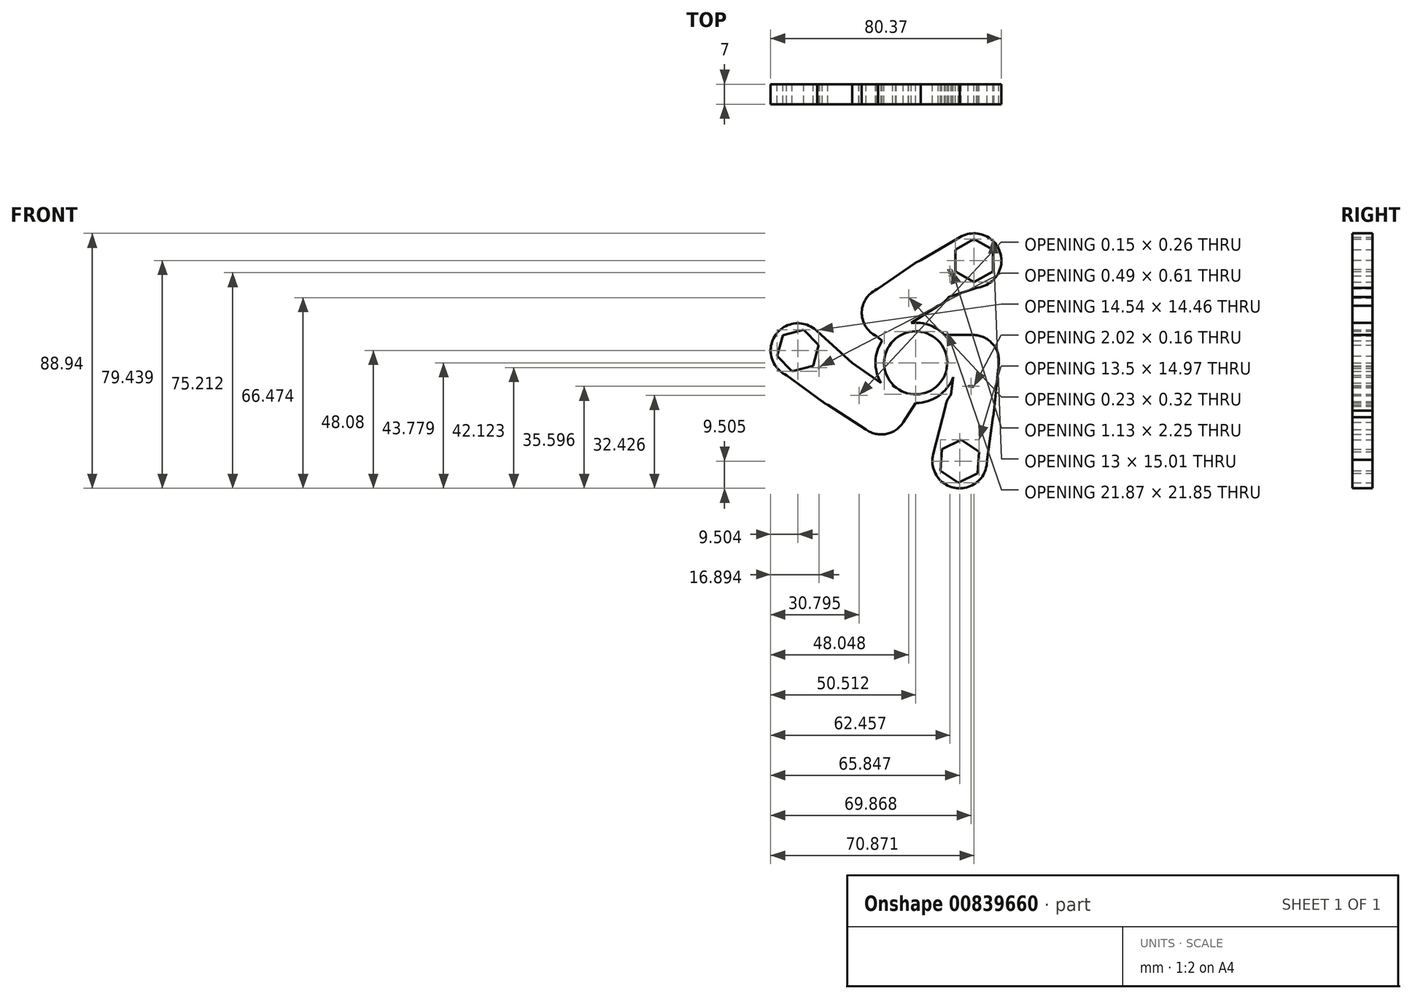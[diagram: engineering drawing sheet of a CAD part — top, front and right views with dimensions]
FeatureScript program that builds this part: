
annotation { "Feature Type Name" : "Feature", "Feature Type Description" : "" }
export const myFeature = defineFeature(function(context is Context, id is Id, definition is map)
    precondition{}
    {
        {
            var Q0;
            Q0=qCreatedBy(makeId("Front.planeOp"),FACE);
            var sketch = newSketch(context, id + "F0", { "sketchPlane" : qUnion([Q0])});
            skCircle(sketch, "E0", {"center": v(0, 0) * mm, "radius": 11 * mm});
            skCircle(sketch, "E1", {"center": v(0, 0) * mm, "radius": 14 * mm});
            skCircle(sketch, "E2", {"center": v(-12, -15.97) * mm, "radius": 9 * mm});
            skPoint(sketch, "E2.first.point", {"position": v(-3.32, -13.6) * mm});
            skPoint(sketch, "E2.second.point", {"position": v(-12.14, -6.97) * mm});
            skPoint(sketch, "E2.third.point", {"position": v(-19.3, -10.7) * mm});
            skCircle(sketch, "E3", {"center": v(-27.02, -6.98) * mm, "radius": 8.5 * mm});
            skPoint(sketch, "E3.first.point", {"position": v(-19.65, -11.22) * mm});
            skPoint(sketch, "E3.second.point", {"position": v(-19.8, -11.47) * mm});
            skPoint(sketch, "E3.third.point", {"position": v(-19.3, -3.4) * mm});
            skLineSegment(sketch, "E4", {"start": v(-12.14, -6.97) * mm, "end": v(-22.16, 0) * mm});
            skLineSegment(sketch, "E5", {"start": v(-4.35, -20.7) * mm, "end": v(0, -14) * mm});
            skCircle(sketch, "E6", {"center": v(19.99, 0.74) * mm, "radius": 9 * mm});
            skPoint(sketch, "E6.first.point", {"position": v(12.66, 5.97) * mm});
            skPoint(sketch, "E6.second.point", {"position": v(13.07, -5.02) * mm});
            skPoint(sketch, "E6.third.point", {"position": v(20.36, -8.25) * mm});
            skCircle(sketch, "E7", {"center": v(18.75, -16.6) * mm, "radius": 8.5 * mm});
            skPoint(sketch, "E7.second.point", {"position": v(12.37, -10.97) * mm});
            skPoint(sketch, "E7.third.point", {"position": v(20.36, -24.94) * mm});
            skLineSegment(sketch, "E8", {"start": v(13.07, -5.02) * mm, "end": v(12.37, -10.97) * mm});
            skLineSegment(sketch, "E9", {"start": v(27.25, -16.6) * mm, "end": v(28.96, 0) * mm});
            skLineSegment(sketch, "E10", {"start": v(0, 0) * mm, "end": v(-17.27, -23.27) * mm});
            skLineSegment(sketch, "E11", {"start": v(-17.27, -23.27) * mm, "end": v(-32.51, -13.46) * mm});
            skLineSegment(sketch, "E12", {"start": v(19.99, 0.74) * mm, "end": v(19.99, 9.74) * mm});
            skLineSegment(sketch, "E13", {"start": v(19.99, 9.74) * mm, "end": v(10.05, 9.74) * mm});
            skCircle(sketch, "E14", {"center": v(-9.78, 17.45) * mm, "radius": 9 * mm});
            skPoint(sketch, "E14.first.point", {"position": v(-11.09, 8.54) * mm});
            skPoint(sketch, "E14.second.point", {"position": v(-1.5, 13.92) * mm});
            skPoint(sketch, "E14.third.point", {"position": v(-11.33, 26.31) * mm});
            skCircle(sketch, "E15", {"center": v(4.42, 27.67) * mm, "radius": 8.5 * mm});
            skPoint(sketch, "E15.first.point", {"position": v(-2.59, 22.86) * mm});
            skPoint(sketch, "E15.second.point", {"position": v(7.8, 19.87) * mm});
            skPoint(sketch, "E15.third.point", {"position": v(12.92, 27.48) * mm});
            skLineSegment(sketch, "E16", {"start": v(7.8, 19.87) * mm, "end": v(-1.5, 13.92) * mm});
            skLineSegment(sketch, "E17", {"start": v(-16.53, 23.4) * mm, "end": v(0, 34.95) * mm});
            skLineSegment(sketch, "E18", {"start": v(-16.92, 11.98) * mm, "end": v(-11.68, 7.72) * mm});
            skCircle(sketch, "E19", {"center": v(15.33, -34.27) * mm, "radius": 9.5 * mm});
            skPoint(sketch, "E19.first.point", {"position": v(17.13, -24.94) * mm});
            skPoint(sketch, "E19.second.point", {"position": v(13.52, -24.94) * mm});
            skPoint(sketch, "E19.third.point", {"position": v(21.46, -41.52) * mm});
            skLineSegment(sketch, "E20", {"start": v(10.36, -15.19) * mm, "end": v(6.12, -31.93) * mm});
            skLineSegment(sketch, "E21", {"start": v(26.93, -18.9) * mm, "end": v(24.31, -37.35) * mm});
            skCircle(sketch, "E22.cCircle", {"center": v(15.33, -34.27) * mm, "radius": 6.5 * mm, "construction": true});
            skLineSegment(sketch, "E22.0", {"start": v(21.55, -38.47) * mm, "end": v(14.8, -41.75) * mm});
            skLineSegment(sketch, "E22.1", {"start": v(14.8, -41.75) * mm, "end": v(8.58, -37.55) * mm});
            skLineSegment(sketch, "E22.2", {"start": v(8.58, -37.55) * mm, "end": v(9.1, -30.06) * mm});
            skLineSegment(sketch, "E22.3", {"start": v(9.1, -30.06) * mm, "end": v(15.86, -26.78) * mm});
            skLineSegment(sketch, "E22.4", {"start": v(15.86, -26.78) * mm, "end": v(22.08, -30.98) * mm});
            skLineSegment(sketch, "E22.5", {"start": v(22.08, -30.98) * mm, "end": v(21.55, -38.47) * mm});
            skPoint(sketch, "E22.0.midPoint", {"position": v(18.17, -40.11) * mm});
            skCircle(sketch, "E23", {"center": v(-41.02, 4.31) * mm, "radius": 9.5 * mm});
            skPoint(sketch, "E23.first.point", {"position": v(-33.87, -1.95) * mm});
            skPoint(sketch, "E23.second.point", {"position": v(-32.06, 7.5) * mm});
            skPoint(sketch, "E23.third.point", {"position": v(-46.5, 12.06) * mm});
            skLineSegment(sketch, "E24", {"start": v(-48.07, -2.05) * mm, "end": v(-32.51, -13.46) * mm});
            skLineSegment(sketch, "E25", {"start": v(-34.3, 11.03) * mm, "end": v(-22.16, 0) * mm});
            skCircle(sketch, "E26.cCircle", {"center": v(-41.02, 4.31) * mm, "radius": 6.5 * mm, "construction": true});
            skLineSegment(sketch, "E26.0", {"start": v(-48.28, 2.44) * mm, "end": v(-46.27, 9.67) * mm});
            skLineSegment(sketch, "E26.1", {"start": v(-46.27, 9.67) * mm, "end": v(-39, 11.54) * mm});
            skLineSegment(sketch, "E26.2", {"start": v(-39, 11.54) * mm, "end": v(-33.75, 6.19) * mm});
            skLineSegment(sketch, "E26.3", {"start": v(-33.75, 6.19) * mm, "end": v(-35.76, -1.05) * mm});
            skLineSegment(sketch, "E26.4", {"start": v(-35.76, -1.05) * mm, "end": v(-43.03, -2.92) * mm});
            skLineSegment(sketch, "E26.5", {"start": v(-43.03, -2.92) * mm, "end": v(-48.28, 2.44) * mm});
            skPoint(sketch, "E26.0.midPoint", {"position": v(-47.28, 6.05) * mm});
            skCircle(sketch, "E27", {"center": v(20.35, 35.67) * mm, "radius": 9.5 * mm});
            skPoint(sketch, "E27.first.point", {"position": v(11.37, 32.57) * mm});
            skPoint(sketch, "E27.second.point", {"position": v(25.43, 27.64) * mm});
            skPoint(sketch, "E27.third.point", {"position": v(23.02, 44.79) * mm});
            skLineSegment(sketch, "E28", {"start": v(25.43, 27.64) * mm, "end": v(11.5, 22.95) * mm});
            skLineSegment(sketch, "E29", {"start": v(15.68, 43.94) * mm, "end": v(1.78, 35.75) * mm});
            skCircle(sketch, "E30.cCircle", {"center": v(20.35, 35.67) * mm, "radius": 6.5 * mm, "construction": true});
            skLineSegment(sketch, "E30.0", {"start": v(13.85, 31.92) * mm, "end": v(13.85, 39.42) * mm});
            skLineSegment(sketch, "E30.1", {"start": v(13.85, 39.42) * mm, "end": v(20.35, 43.17) * mm});
            skLineSegment(sketch, "E30.2", {"start": v(20.35, 43.17) * mm, "end": v(26.85, 39.42) * mm});
            skLineSegment(sketch, "E30.3", {"start": v(26.85, 39.42) * mm, "end": v(26.85, 31.92) * mm});
            skLineSegment(sketch, "E30.4", {"start": v(26.85, 31.92) * mm, "end": v(20.35, 28.16) * mm});
            skLineSegment(sketch, "E30.5", {"start": v(20.35, 28.16) * mm, "end": v(13.85, 31.92) * mm});
            skPoint(sketch, "E30.0.midPoint", {"position": v(13.85, 35.67) * mm});
            skLineSegment(sketch, "E31", {"start": v(-7.96, -7.93) * mm, "end": v(-4.88, -9.86) * mm});
            skSolve(sketch);
        }
        {
            var Q0;
            Q0 = qSketchRegion(id + "F0", true);
            var Q1;
            {var subQ0=sQuery(id+"F0.wireOp",EDGE,"E10");var subQ1=sQuery(id+"F0.wireOp",EDGE,"E0");var subQ2=makeQuery(id+"F0.imprint","INTERSECT",VERTEX,{"derivedFrom":[subQ1,subQ0]});Q1=makeQuery(id+"F0.imprint","IMPRINT",FACE,{"disambiguationData":[TD([[makeQuery(id+"F0.imprint","IMPRINT",EDGE,{"disambiguationData":[TD([[subQ2,-1.0]])],"derivedFrom":subQ1}),-1.0]])]});}
            extrude(context, id + "F1", {"entities" : qUnion([Q0, Q1]), "depth" : 7 * mm, "offsetDistance" : 25 * mm});
        }
    });
